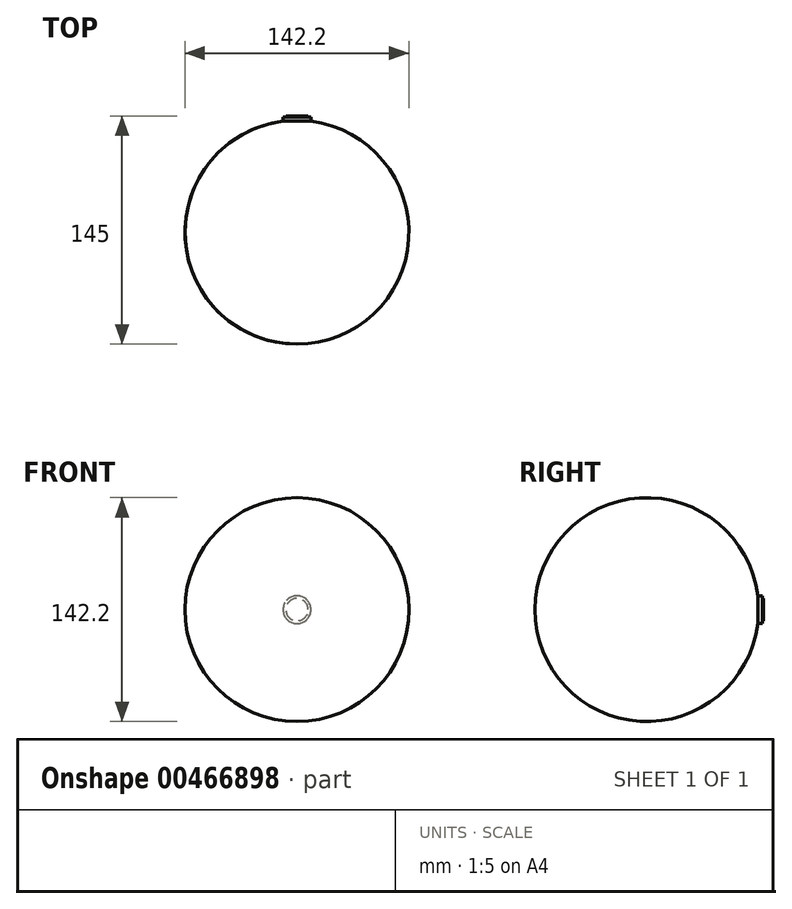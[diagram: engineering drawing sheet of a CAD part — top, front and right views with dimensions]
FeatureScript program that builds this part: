
annotation { "Feature Type Name" : "Feature", "Feature Type Description" : "" }
export const myFeature = defineFeature(function(context is Context, id is Id, definition is map)
    precondition{}
    {
        {
            var Q0;
            Q0=qCreatedBy(makeId("Top.planeOp"),FACE);
            var sketch = newSketch(context, id + "F0", { "sketchPlane" : qUnion([Q0])});
            skArc(sketch, "E0", {"start": v(0, 71.1) * mm, "mid": v(-71.1, 0) * mm, "end": v(0, -71.1) * mm});
            skLineSegment(sketch, "E1", {"start": v(0, 75.97) * mm, "end": v(0, -76.78) * mm});
            skLineSegment(sketch, "E2", {"start": v(-8.85, 70.55) * mm, "end": v(-8.85, 73.28) * mm});
            skLineSegment(sketch, "E3", {"start": v(-8.85, 73.28) * mm, "end": v(0, 73.28) * mm});
            skLineSegment(sketch, "E4", {"start": v(-7.1, 73.28) * mm, "end": v(-7.1, 73.9) * mm});
            skLineSegment(sketch, "E5", {"start": v(-7.1, 73.9) * mm, "end": v(0, 73.9) * mm});
            skSolve(sketch);
        }
        {
            var Q0;
            Q0 = qSketchRegion(id + "F0", true);
            var Q1;
            Q1=sQuery(id+"F0.wireOp",EDGE,"E1");
            revolve(context, id + "F1", {"entities" : qUnion([Q0]), "axis" : qUnion([Q1]), "revolveType" : RevolveType.FULL});
        }
    });
